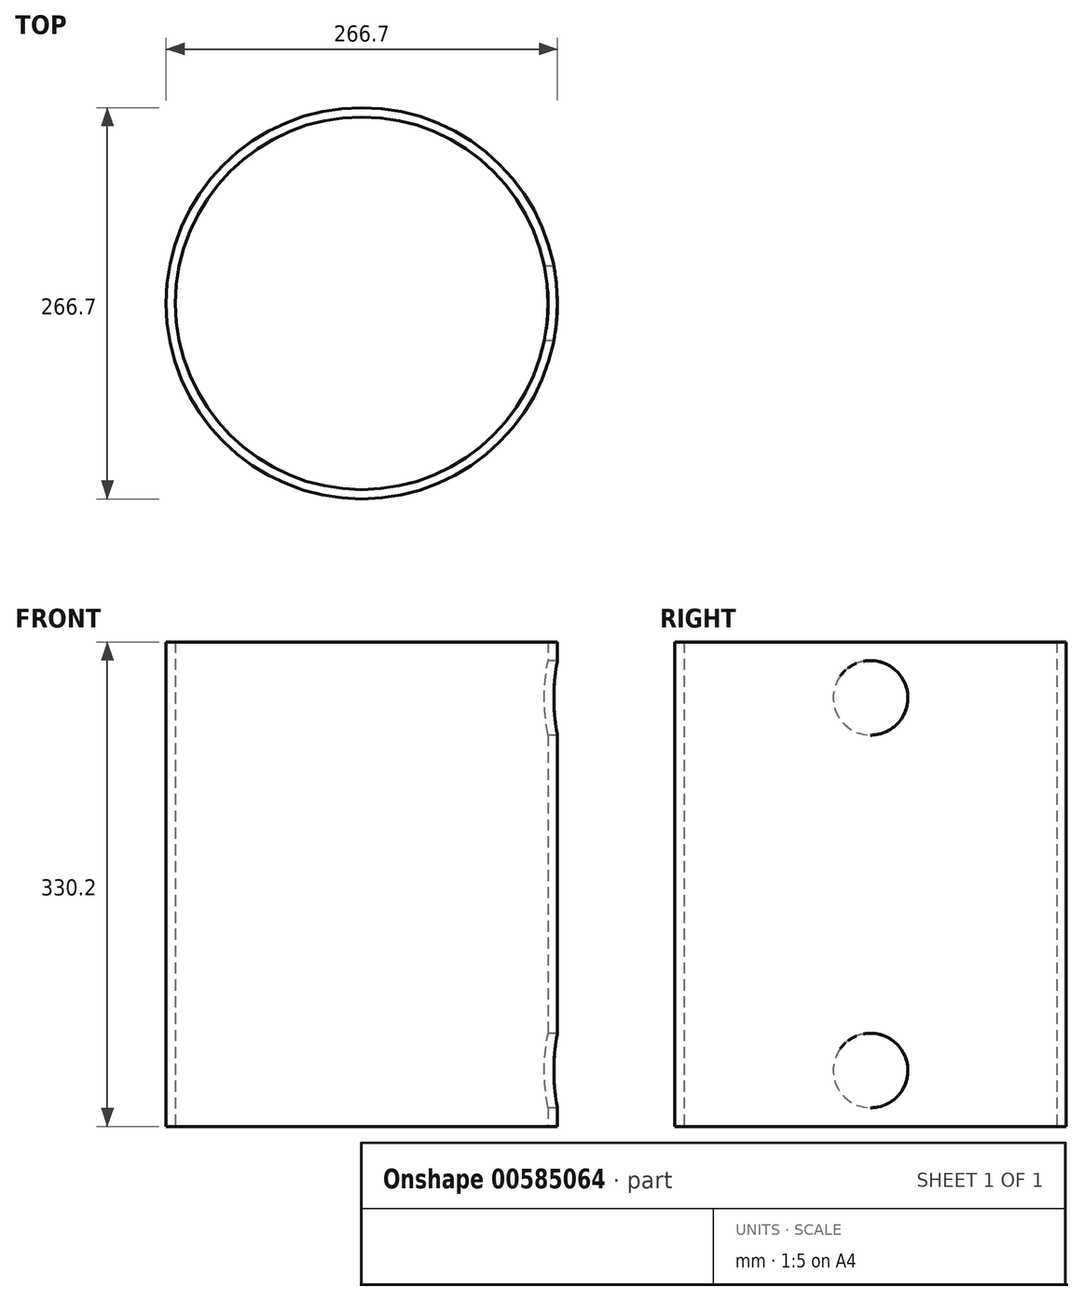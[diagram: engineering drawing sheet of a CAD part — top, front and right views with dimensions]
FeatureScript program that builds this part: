
annotation { "Feature Type Name" : "Feature", "Feature Type Description" : "" }
export const myFeature = defineFeature(function(context is Context, id is Id, definition is map)
    precondition{}
    {
        {
            var Q0;
            Q0=qCreatedBy(makeId("Top.planeOp"),FACE);
            var sketch = newSketch(context, id + "F0", { "sketchPlane" : qUnion([Q0])});
            skCircle(sketch, "E0", {"center": v(0, 0) * mm, "radius": 127 * mm});
            skCircle(sketch, "E1", {"center": v(0, 0) * mm, "radius": 133.35 * mm});
            skSolve(sketch);
        }
        {
            var Q0;
            Q0 = qSketchRegion(id + "F0", true);
            extrude(context, id + "F1", {"entities" : qUnion([Q0]), "depth" : 330.2 * mm, "offsetDistance" : 25.4 * mm});
        }
        {
            var Q0;
            Q0=qCreatedBy(makeId("Front.planeOp"),FACE);
            var sketch = newSketch(context, id + "F2", { "sketchPlane" : qUnion([Q0])});
            skLineSegment(sketch, "E2", {"start": v(0, 0) * mm, "end": v(0, 31.75) * mm, "construction": true});
            skLineSegment(sketch, "E3", {"start": v(0, 31.75) * mm, "end": v(88.9, 31.75) * mm, "construction": true});
            skLineSegment(sketch, "E4", {"start": v(0, 31.75) * mm, "end": v(-88.9, 31.75) * mm, "construction": true});
            skCircle(sketch, "E5", {"center": v(-88.9, 31.75) * mm, "radius": 25.4 * mm});
            skCircle(sketch, "E6", {"center": v(88.9, 31.75) * mm, "radius": 25.4 * mm});
            skSolve(sketch);
        }
        {
            var Q0;
            Q0=qCreatedBy(makeId("Right.planeOp"),FACE);
            var sketch = newSketch(context, id + "F3", { "sketchPlane" : qUnion([Q0])});
            skLineSegment(sketch, "E7", {"start": v(0, 0) * mm, "end": v(0, 12.7) * mm, "construction": true});
            skLineSegment(sketch, "E8", {"start": v(0, 12.7) * mm, "end": v(0, 63.5) * mm, "construction": true});
            skLineSegment(sketch, "E9", {"start": v(0, 63.5) * mm, "end": v(0, 266.7) * mm, "construction": true});
            skLineSegment(sketch, "E10", {"start": v(0, 266.7) * mm, "end": v(0, 317.5) * mm, "construction": true});
            skCircle(sketch, "E11", {"center": v(0, 38.1) * mm, "radius": 25.4 * mm});
            skCircle(sketch, "E12", {"center": v(0, 292.1) * mm, "radius": 25.4 * mm});
            skSolve(sketch);
        }
        {
            var Q0;
            Q0 = qSketchRegion(id + "F3", true);
            extrude(context, id + "F4", {"entities" : qUnion([Q0]), "operationType" : NewBodyOperationType.REMOVE, "depth" : 508 * mm, "offsetDistance" : 25.4 * mm});
        }
    });
